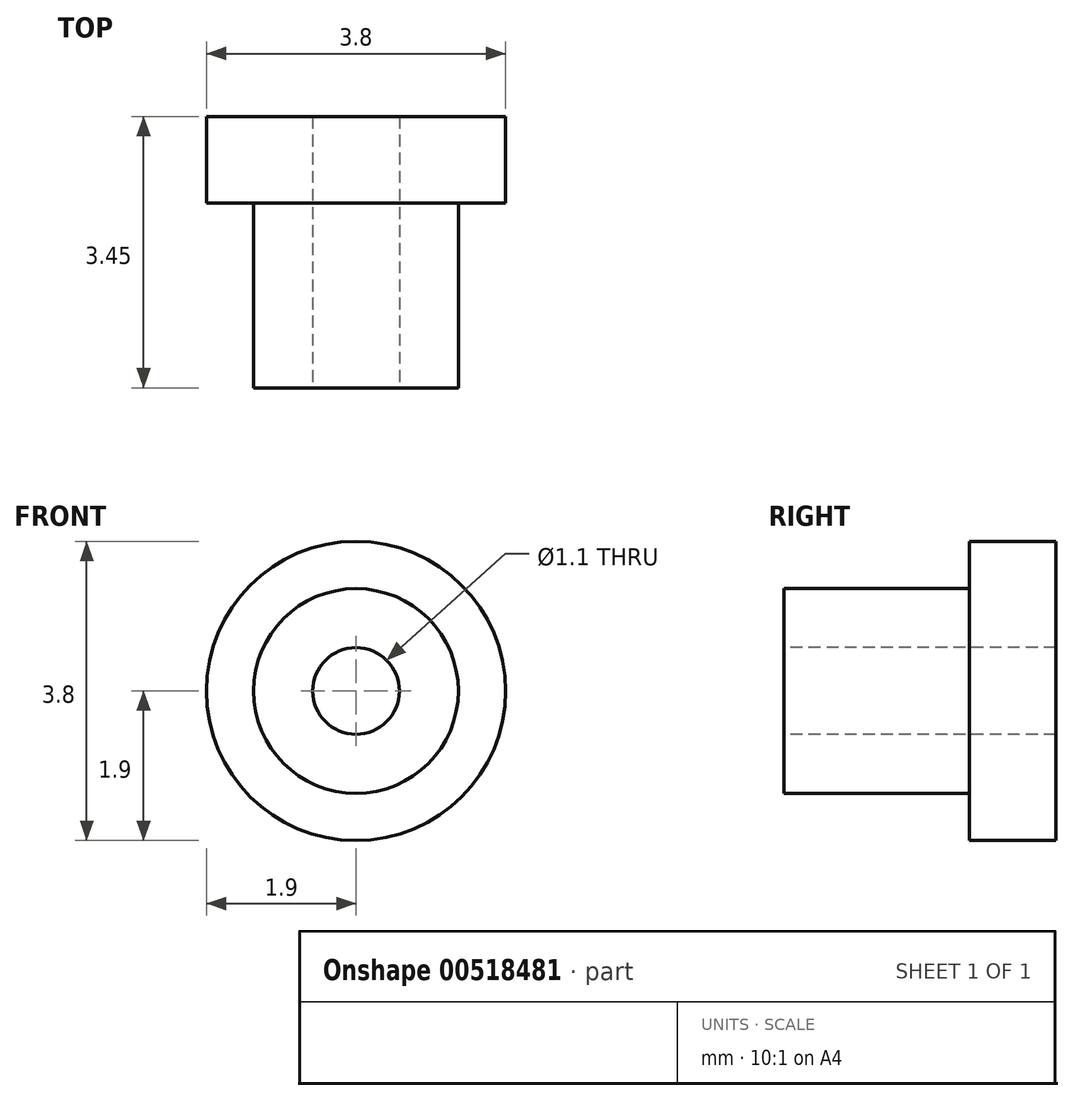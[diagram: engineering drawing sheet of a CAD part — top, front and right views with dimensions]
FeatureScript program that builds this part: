
annotation { "Feature Type Name" : "Feature", "Feature Type Description" : "" }
export const myFeature = defineFeature(function(context is Context, id is Id, definition is map)
    precondition{}
    {
        {
            var Q0;
            Q0=qCreatedBy(makeId("Right.planeOp"),FACE);
            var sketch = newSketch(context, id + "F0", { "sketchPlane" : qUnion([Q0])});
            skLineSegment(sketch, "E0", {"start": v(2.58, 0.55) * mm, "end": v(-0.87, 0.55) * mm});
            skLineSegment(sketch, "E1", {"start": v(-0.87, 0.55) * mm, "end": v(2.58, 0.55) * mm});
            skLineSegment(sketch, "E2", {"start": v(2.58, 0.55) * mm, "end": v(2.58, 1.9) * mm});
            skLineSegment(sketch, "E3", {"start": v(2.58, 1.9) * mm, "end": v(1.48, 1.9) * mm});
            skLineSegment(sketch, "E4", {"start": v(1.48, 1.9) * mm, "end": v(1.48, 1.3) * mm});
            skLineSegment(sketch, "E5", {"start": v(1.48, 1.3) * mm, "end": v(-0.87, 1.3) * mm});
            skLineSegment(sketch, "E6", {"start": v(-0.87, 1.3) * mm, "end": v(-0.87, 0.55) * mm});
            skLineSegment(sketch, "E7", {"start": v(-1.87, 0) * mm, "end": v(1.85, 0) * mm, "construction": true});
            skLineSegment(sketch, "E8.MirrorCS", {"start": v(-0.87, -0.55) * mm, "end": v(2.58, -0.55) * mm, "construction": true});
            skLineSegment(sketch, "E9.MirrorCS", {"start": v(1.48, -1.3) * mm, "end": v(-0.87, -1.3) * mm, "construction": true});
            skLineSegment(sketch, "E10.MirrorCS", {"start": v(2.58, -1.9) * mm, "end": v(1.48, -1.9) * mm, "construction": true});
            skSolve(sketch);
        }
        {
            var Q0;
            Q0 = qSketchRegion(id + "F0", true);
            var Q1;
            Q1=sQuery(id+"F0.wireOp",EDGE,"E7");
            revolve(context, id + "F1", {"entities" : qUnion([Q0]), "axis" : qUnion([Q1]), "revolveType" : RevolveType.FULL});
        }
    });
